# Revit family: NLRS_57_DUA_UN_round smokesensor ug_sacs
name_source: partatom
category: Duct Accessories
units: mm (PartAtom-declared; Revit-internal decimal feet)

## family parameters
Always vertical = Yes
Cut with Voids When Loaded = No
Part Type = Breaks Into
Round Connector Dimension = Use Diameter
Shared = No
Work Plane-Based = No

## types (1)
- NLRS_57_DUA_UN_round smokesensor ug_sacs
    Article_Data = UG_Round_Article_Data
    Assembly Code = 57.70
    Casing material = Gegalvaniseerd plaatstaal
    Combo (do not change!) = No
    Description = Ronde rook sensor
    FireRating = 0h
    IfcDescription = Ronde rook sensor
    IfcExportAs = IfcDamperType
    IfcExportType = SMOKE SENSOR
    LoadBearing = No
    Manufacturer = Solid Air Climate Solutions
    Model = Koude rook sensor rond
    NLRS_C_content_datum_uitgifte = 19-01-2022
    NLRS_C_content_provider = Solid Air Climate Systems
    NLRS_C_content_versie = Versie 3.19.00
    NLRS_C_description = Ronde rook sensor
    NLRS_C_niveau ontwikkeling = LOD400
    SACS_Cin_Offst = 42 mm  [stored 0.137795 ft]
    Type Comments = Check flow direction!
    URL = https://solid-air.nl

note: [stored X ft] marks values corroborated as IEEE doubles in the binary element streams (Revit-internal decimal feet)

## geometry (parser evidence)
native form markers: Sweep x15
no freeform markers — native parametric forms only
